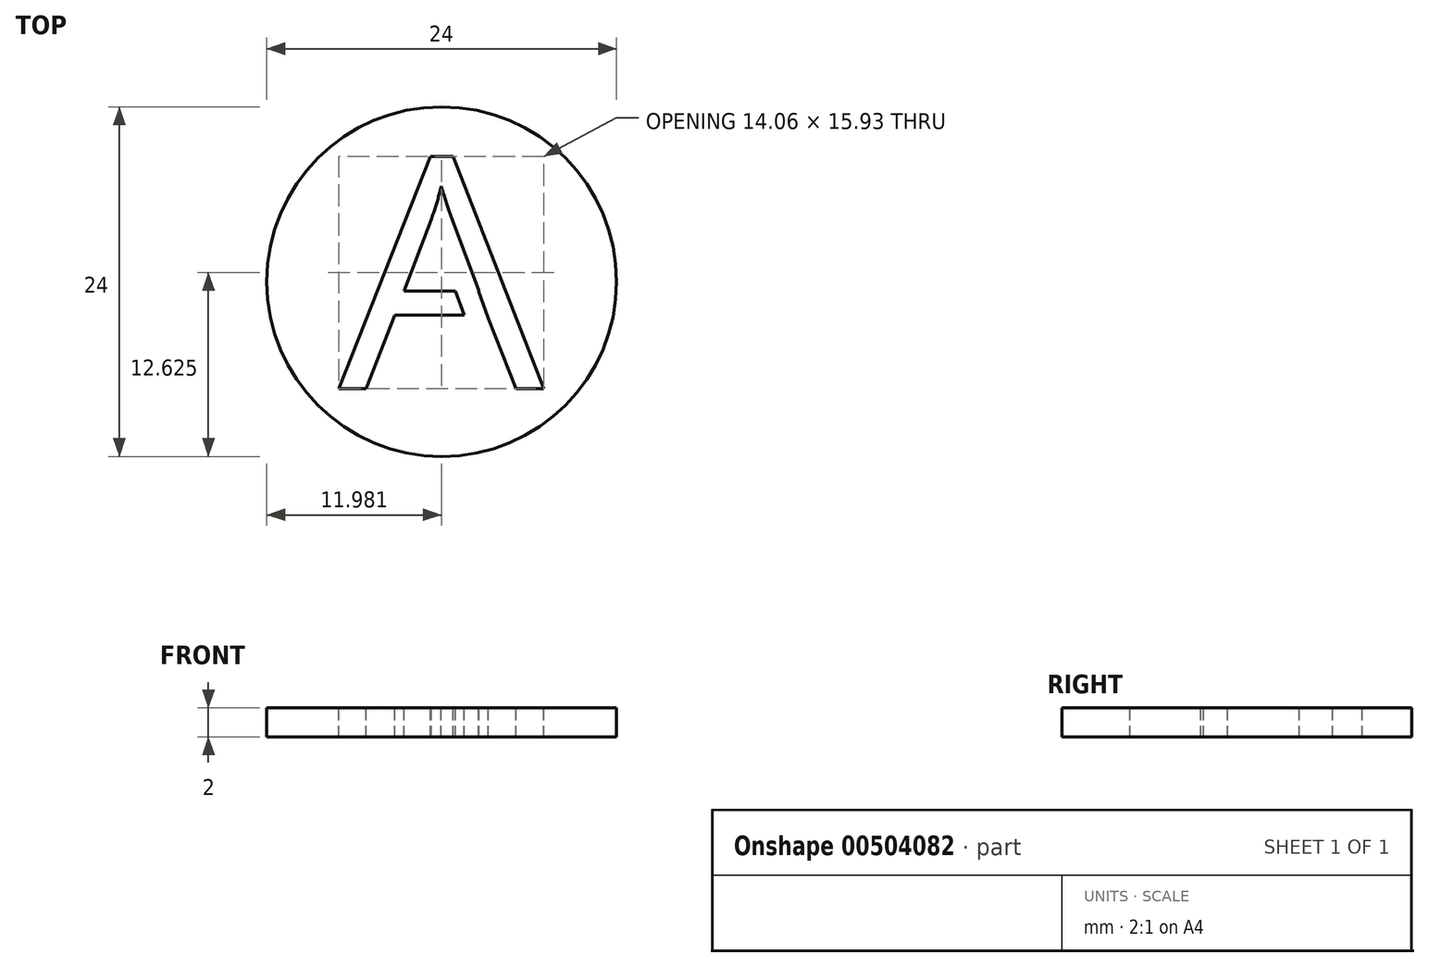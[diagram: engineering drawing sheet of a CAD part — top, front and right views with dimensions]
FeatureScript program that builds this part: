
annotation { "Feature Type Name" : "Feature", "Feature Type Description" : "" }
export const myFeature = defineFeature(function(context is Context, id is Id, definition is map)
    precondition{}
    {
        {
            var Q0;
            Q0=qCreatedBy(makeId("Top.planeOp"),FACE);
            var sketch = newSketch(context, id + "F0", { "sketchPlane" : qUnion([Q0])});
            skCircle(sketch, "E0", {"center": v(0, 0) * mm, "radius": 12 * mm});
            skSolve(sketch);
        }
        {
            var Q0;
            Q0=qSketchRegion(id+"F0",true);
            extrude(context, id + "F1", {"entities" : qUnion([Q0]), "depth" : 2 * mm});
        }
        {
            var Q0;
            Q0=makeQuery(id+"F1.opExtrude","CAP_FACE",FACE,{"disambiguationData":[OSD([sQuery(id+"F0.wireOp",EDGE,"E0")])],"isStart":false});
            var sketch = newSketch(context, id + "F2", { "sketchPlane" : qUnion([Q0])});
            skText(sketch, "E1", { "text": "A", "fontName": "OpenSans-Regular.ttf"});
            skLineSegment(sketch, "E2", {"start": v(-2.54, -0.52) * mm, "end": v(-3.4, -2.7) * mm});
            skLineSegment(sketch, "E3", {"start": v(2.26, 0.14) * mm, "end": v(3.26, -2.64) * mm});
            skLineSegment(sketch, "E4", {"start": v(-1.04, -0.52) * mm, "end": v(-1.9, -2.7) * mm});
            skLineSegment(sketch, "E5", {"start": v(0.82, -0.3) * mm, "end": v(1.66, -2.64) * mm});
            const initialGuessF2  = {"E1": [-0.00705, -0.00734, 1, 0, 0.016]};
            skSetInitialGuess(sketch, initialGuessF2);
            skSolve(sketch);
        }
        {
            var Q0;
            {var subQ0=sQuery(id+"F2.wireOp",EDGE,"E5");var subQ1=sQuery(id+"F2.wireOp",EDGE,"E1.sketch_text.stroke-1");var subQ2=makeQuery(id+"F2.imprint","INTERSECT",VERTEX,{"derivedFrom":[subQ1,subQ0]});Q0=makeQuery(id+"F2.imprint","IMPRINT",FACE,{"disambiguationData":[TD([[makeQuery(id+"F2.imprint","IMPRINT",EDGE,{"disambiguationData":[TD([[subQ2,-1.0]])],"derivedFrom":subQ1}),-1.0]])]});}
            var Q1;
            {var subQ6=sQuery(id+"F2.wireOp",EDGE,"E1.sketch_text.stroke-3");Q1=makeQuery(id+"F2.imprint","IMPRINT",FACE,{"disambiguationData":[TD([[makeQuery(id+"F2.imprint","IMPRINT",EDGE,{"derivedFrom":subQ6}),-1.0]])]});}
            extrude(context, id + "F3", {"entities" : qUnion([Q0, Q1]), "operationType" : NewBodyOperationType.REMOVE, "oppositeDirection" : true, "depth" : 25 * mm, "offsetDistance" : 25 * mm});
        }
    });
